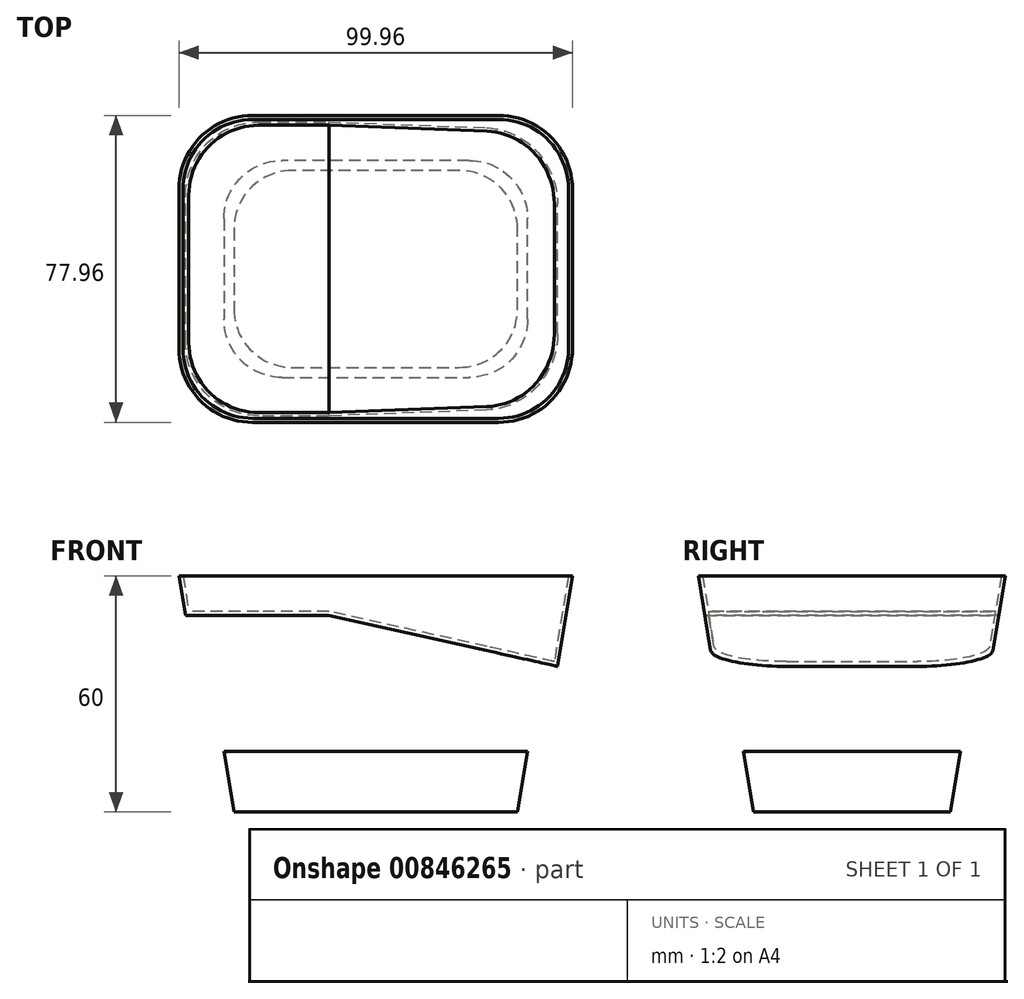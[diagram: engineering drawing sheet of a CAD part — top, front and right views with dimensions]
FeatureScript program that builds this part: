
annotation { "Feature Type Name" : "Feature", "Feature Type Description" : "" }
export const myFeature = defineFeature(function(context is Context, id is Id, definition is map)
    precondition{}
    {
        {
            var Q0;
            Q0=qCreatedBy(makeId("Front.planeOp"),FACE);
            var sketch = newSketch(context, id + "F0", { "sketchPlane" : qUnion([Q0])});
            skLineSegment(sketch, "E0", {"start": v(-36, 0) * mm, "end": v(36, 0) * mm});
            skLineSegment(sketch, "E1", {"start": v(36, 0) * mm, "end": v(42.3, 37.87) * mm});
            skLineSegment(sketch, "E2", {"start": v(46.2, 37) * mm, "end": v(50.02, 60) * mm});
            skLineSegment(sketch, "E3", {"start": v(50.02, 60) * mm, "end": v(-49.98, 60) * mm});
            skLineSegment(sketch, "E4", {"start": v(-49.98, 60) * mm, "end": v(-48.31, 50) * mm});
            skLineSegment(sketch, "E5", {"start": v(-48.31, 50) * mm, "end": v(-11.98, 50) * mm});
            skLineSegment(sketch, "E6", {"start": v(-11.98, 50) * mm, "end": v(46.2, 37) * mm});
            skLineSegment(sketch, "E7", {"start": v(-44.31, 50) * mm, "end": v(-36, 0) * mm});
            skLineSegment(sketch, "E8", {"start": v(-53.76, 50) * mm, "end": v(-51.33, 15.4) * mm});
            skLineSegment(sketch, "E9", {"start": v(-51.33, 15.4) * mm, "end": v(59.27, 15.4) * mm});
            skLineSegment(sketch, "E10", {"start": v(59.27, 15.4) * mm, "end": v(46.2, 37) * mm});
            skLineSegment(sketch, "E11", {"start": v(-53.76, 50) * mm, "end": v(-48.31, 50) * mm});
            skSolve(sketch);
        }
        {
            var Q0;
            Q0=qCreatedBy(makeId("Top.planeOp"),FACE);
            var sketch = newSketch(context, id + "F1", { "sketchPlane" : qUnion([Q0])});
            skLineSegment(sketch, "E12", {"start": v(-36, 25) * mm, "end": v(-36, -25) * mm});
            skLineSegment(sketch, "E13", {"start": v(-36, -25) * mm, "end": v(36, -25) * mm});
            skLineSegment(sketch, "E14", {"start": v(36, -25) * mm, "end": v(36, 25) * mm});
            skLineSegment(sketch, "E15", {"start": v(36, 25) * mm, "end": v(-36, 25) * mm});
            skSolve(sketch);
        }
        {
            var Q0;
            Q0=sQuery(id+"F0.wireOp",EDGE,"E5");
            var Q1;
            Q1=qCreatedBy(makeId("Top.planeOp"),FACE);
            cPlane(context, id + "F2", {"entities" : qUnion([Q0, Q1]), "cplaneType" : CPlaneType.LINE_ANGLE, "offset" : 25 * mm, "angle" : 0 * degree, "width" : 150 * mm, "height" : 150 * mm});
        }
        {
            var Q0;
            Q0=qCreatedBy(id+"F2.planeOp",FACE);
            var sketch = newSketch(context, id + "F3", { "sketchPlane" : qUnion([Q0])});
            skLineSegment(sketch, "E16.0", {"start": v(44.31, -33.31) * mm, "end": v(-44.31, -33.31) * mm});
            skLineSegment(sketch, "E16.1", {"start": v(44.31, 33.31) * mm, "end": v(44.31, -33.31) * mm});
            skLineSegment(sketch, "E16.2", {"start": v(-44.31, 33.31) * mm, "end": v(44.31, 33.31) * mm});
            skLineSegment(sketch, "E16.3", {"start": v(-44.31, -33.31) * mm, "end": v(-44.31, 33.31) * mm});
            skSolve(sketch);
        }
        {
            var Q0;
            Q0=makeQuery(id+"F1.imprint","IMPRINT",FACE,{"disambiguationData":[TD([[makeQuery(id+"F1.imprint","IMPRINT",EDGE,{"derivedFrom":sQuery(id+"F1.wireOp",EDGE,"E12")}),1.0]])]});
            var Q1;
            Q1=makeQuery(id+"F3.imprint","IMPRINT",FACE,{"disambiguationData":[TD([[makeQuery(id+"F3.imprint","IMPRINT",EDGE,{"derivedFrom":sQuery(id+"F3.wireOp",EDGE,"E16.0")}),-1.0]])]});
            loft(context, id + "F4", {"sheetProfilesArray" : [{ "sheetProfileEntities" : qUnion([Q0]) }, { "sheetProfileEntities" : qUnion([Q1]) }]});
        }
        {
            var Q0;
            {var subQ3=sQuery(id+"F0.wireOp",EDGE,"E2");Q0=makeQuery(id+"F0.imprint","IMPRINT",FACE,{"disambiguationData":[TD([[makeQuery(id+"F0.imprint","IMPRINT",EDGE,{"derivedFrom":subQ3}),1.0]])]});}
            extrude(context, id + "F5", {"entities" : qUnion([Q0]), "operationType" : NewBodyOperationType.REMOVE, "endBound" : BoundingType.SYMMETRIC, "oppositeDirection" : true, "depth" : 100 * mm, "offsetDistance" : 25 * mm});
        }
        {
            var Q0;
            Q0=sQuery(id+"F0.wireOp",VERTEX,"E2.start");
            var Q1;
            Q1=qCreatedBy(makeId("Top.planeOp"),FACE);
            cPlane(context, id + "F6", {"entities" : qUnion([Q0, Q1]), "cplaneType" : CPlaneType.PLANE_POINT, "offset" : 25 * mm, "width" : 150 * mm, "height" : 150 * mm});
        }
        {
            var Q0;
            Q0=qCreatedBy(id+"F6.planeOp",FACE);
            var sketch = newSketch(context, id + "F7", { "sketchPlane" : qUnion([Q0])});
            skLineSegment(sketch, "E17.0", {"start": v(46.2, 35.2) * mm, "end": v(-46.2, 35.2) * mm});
            skLineSegment(sketch, "E17.1", {"start": v(46.2, -35.2) * mm, "end": v(46.2, 35.2) * mm});
            skLineSegment(sketch, "E17.2", {"start": v(-46.2, -35.2) * mm, "end": v(46.2, -35.2) * mm});
            skLineSegment(sketch, "E17.3", {"start": v(-46.2, 35.2) * mm, "end": v(-46.2, -35.2) * mm});
            skSolve(sketch);
        }
        {
            var Q0;
            Q0=qCreatedBy(makeId("Top.planeOp"),FACE);
            var Q1;
            Q1=sQuery(id+"F0.wireOp",VERTEX,"E2.end");
            cPlane(context, id + "F8", {"entities" : qUnion([Q0, Q1]), "cplaneType" : CPlaneType.PLANE_POINT, "offset" : 25 * mm, "width" : 150 * mm, "height" : 150 * mm});
        }
        {
            var Q0;
            Q0=qCreatedBy(id+"F8.planeOp",FACE);
            var sketch = newSketch(context, id + "F9", { "sketchPlane" : qUnion([Q0])});
            skLineSegment(sketch, "E18.0", {"start": v(49.98, 38.98) * mm, "end": v(-49.98, 38.98) * mm});
            skLineSegment(sketch, "E18.1", {"start": v(49.98, -38.98) * mm, "end": v(49.98, 38.98) * mm});
            skLineSegment(sketch, "E18.2", {"start": v(-49.98, -38.98) * mm, "end": v(49.98, -38.98) * mm});
            skLineSegment(sketch, "E18.3", {"start": v(-49.98, 38.98) * mm, "end": v(-49.98, -38.98) * mm});
            skSolve(sketch);
        }
        {
            var Q0;
            Q0=makeQuery(id+"F9.imprint","IMPRINT",FACE,{"disambiguationData":[TD([[makeQuery(id+"F9.imprint","IMPRINT",EDGE,{"derivedFrom":sQuery(id+"F9.wireOp",EDGE,"E18.0")}),1.0]])]});
            var Q1;
            Q1=makeQuery(id+"F7.imprint","IMPRINT",FACE,{"disambiguationData":[TD([[makeQuery(id+"F7.imprint","IMPRINT",EDGE,{"derivedFrom":sQuery(id+"F7.wireOp",EDGE,"E17.0")}),1.0]])]});
            loft(context, id + "F10", {"sheetProfilesArray" : [{ "sheetProfileEntities" : qUnion([Q0]) }, { "sheetProfileEntities" : qUnion([Q1]) }]});
        }
        {
            var Q0;
            {var subQ0=sQuery(id+"F0.wireOp",EDGE,"E8");Q0=makeQuery(id+"F0.imprint","IMPRINT",FACE,{"disambiguationData":[TD([[makeQuery(id+"F0.imprint","IMPRINT",EDGE,{"derivedFrom":subQ0}),1.0]])]});}
            var Q1;
            {var subQ5=sQuery(id+"F0.wireOp",EDGE,"E6");var subQ6=sQuery(id+"F0.wireOp",EDGE,"E1");var subQ7=makeQuery(id+"F0.imprint","INTERSECT",VERTEX,{"derivedFrom":[subQ6,subQ5]});Q1=makeQuery(id+"F0.imprint","IMPRINT",FACE,{"disambiguationData":[TD([[makeQuery(id+"F0.imprint","IMPRINT",EDGE,{"disambiguationData":[TD([[subQ7,1.0]])],"derivedFrom":subQ6}),1.0]])]});}
            var Q2;
            {var subQ5=sQuery(id+"F0.wireOp",EDGE,"E10");Q2=makeQuery(id+"F0.imprint","IMPRINT",FACE,{"disambiguationData":[TD([[makeQuery(id+"F0.imprint","IMPRINT",EDGE,{"derivedFrom":subQ5}),1.0]])]});}
            extrude(context, id + "F11", {"entities" : qUnion([Q0, Q1, Q2]), "operationType" : NewBodyOperationType.REMOVE, "endBound" : BoundingType.SYMMETRIC, "oppositeDirection" : true, "depth" : 100 * mm, "offsetDistance" : 25 * mm});
        }
        {
            var Q0;
            Q0=makeQuery(id+"F4.opLoft","SWEPT_EDGE",EDGE,{"disambiguationData":[OSD([sQuery(id+"F1.wireOp",EDGE,"E12"),sQuery(id+"F1.wireOp",EDGE,"E13"),sQuery(id+"F3.wireOp",EDGE,"E16.2"),sQuery(id+"F3.wireOp",EDGE,"E16.3")])]});
            var Q1;
            Q1=makeQuery(id+"F4.opLoft","SWEPT_EDGE",EDGE,{"disambiguationData":[OSD([sQuery(id+"F1.wireOp",EDGE,"E12"),sQuery(id+"F1.wireOp",EDGE,"E15"),sQuery(id+"F3.wireOp",EDGE,"E16.0"),sQuery(id+"F3.wireOp",EDGE,"E16.3")])]});
            var Q2;
            Q2=makeQuery(id+"F4.opLoft","SWEPT_EDGE",EDGE,{"disambiguationData":[OSD([sQuery(id+"F1.wireOp",EDGE,"E13"),sQuery(id+"F1.wireOp",EDGE,"E14"),sQuery(id+"F3.wireOp",EDGE,"E16.1"),sQuery(id+"F3.wireOp",EDGE,"E16.2")])]});
            var Q3;
            Q3=makeQuery(id+"F4.opLoft","SWEPT_EDGE",EDGE,{"disambiguationData":[OSD([sQuery(id+"F1.wireOp",EDGE,"E14"),sQuery(id+"F1.wireOp",EDGE,"E15"),sQuery(id+"F3.wireOp",EDGE,"E16.0"),sQuery(id+"F3.wireOp",EDGE,"E16.1")])]});
            fillet(context, id + "F12", {"entities" : qUnion([Q0, Q1, Q2, Q3]), "radius" : 15 * mm, "tangentPropagation" : true, "allowEdgeOverflow" : false});
        }
        {
            var Q0;
            Q0=makeQuery(id+"F10.opLoft","SWEPT_EDGE",EDGE,{"disambiguationData":[OSD([sQuery(id+"F7.wireOp",EDGE,"E17.2"),sQuery(id+"F7.wireOp",EDGE,"E17.3"),sQuery(id+"F9.wireOp",EDGE,"E18.2"),sQuery(id+"F9.wireOp",EDGE,"E18.3")])]});
            var Q1;
            Q1=makeQuery(id+"F10.opLoft","SWEPT_EDGE",EDGE,{"disambiguationData":[OSD([sQuery(id+"F7.wireOp",EDGE,"E17.0"),sQuery(id+"F7.wireOp",EDGE,"E17.3"),sQuery(id+"F9.wireOp",EDGE,"E18.0"),sQuery(id+"F9.wireOp",EDGE,"E18.3")])]});
            var Q2;
            Q2=makeQuery(id+"F10.opLoft","SWEPT_EDGE",EDGE,{"disambiguationData":[OSD([sQuery(id+"F7.wireOp",EDGE,"E17.1"),sQuery(id+"F7.wireOp",EDGE,"E17.2"),sQuery(id+"F9.wireOp",EDGE,"E18.1"),sQuery(id+"F9.wireOp",EDGE,"E18.2")])]});
            var Q3;
            Q3=makeQuery(id+"F10.opLoft","SWEPT_EDGE",EDGE,{"disambiguationData":[OSD([sQuery(id+"F7.wireOp",EDGE,"E17.0"),sQuery(id+"F7.wireOp",EDGE,"E17.1"),sQuery(id+"F9.wireOp",EDGE,"E18.0"),sQuery(id+"F9.wireOp",EDGE,"E18.1")])]});
            fillet(context, id + "F13", {"entities" : qUnion([Q0, Q1, Q2, Q3]), "radius" : 19 * mm, "tangentPropagation" : true, "allowEdgeOverflow" : false});
        }
        {
            var Q0;
            Q0=makeQuery(id+"F10.opLoft","CAP_FACE",FACE,{"disambiguationData":[OSD([makeQuery(id+"F9.imprint","IMPRINT",FACE,{"disambiguationData":[TD([[makeQuery(id+"F9.imprint","IMPRINT",EDGE,{"derivedFrom":sQuery(id+"F9.wireOp",EDGE,"E18.0")}),1.0]])]})])],"isStart":true});
            shell(context, id + "F14", {"entities" : qUnion([Q0]), "thickness" : 1 * mm});
        }
    });
